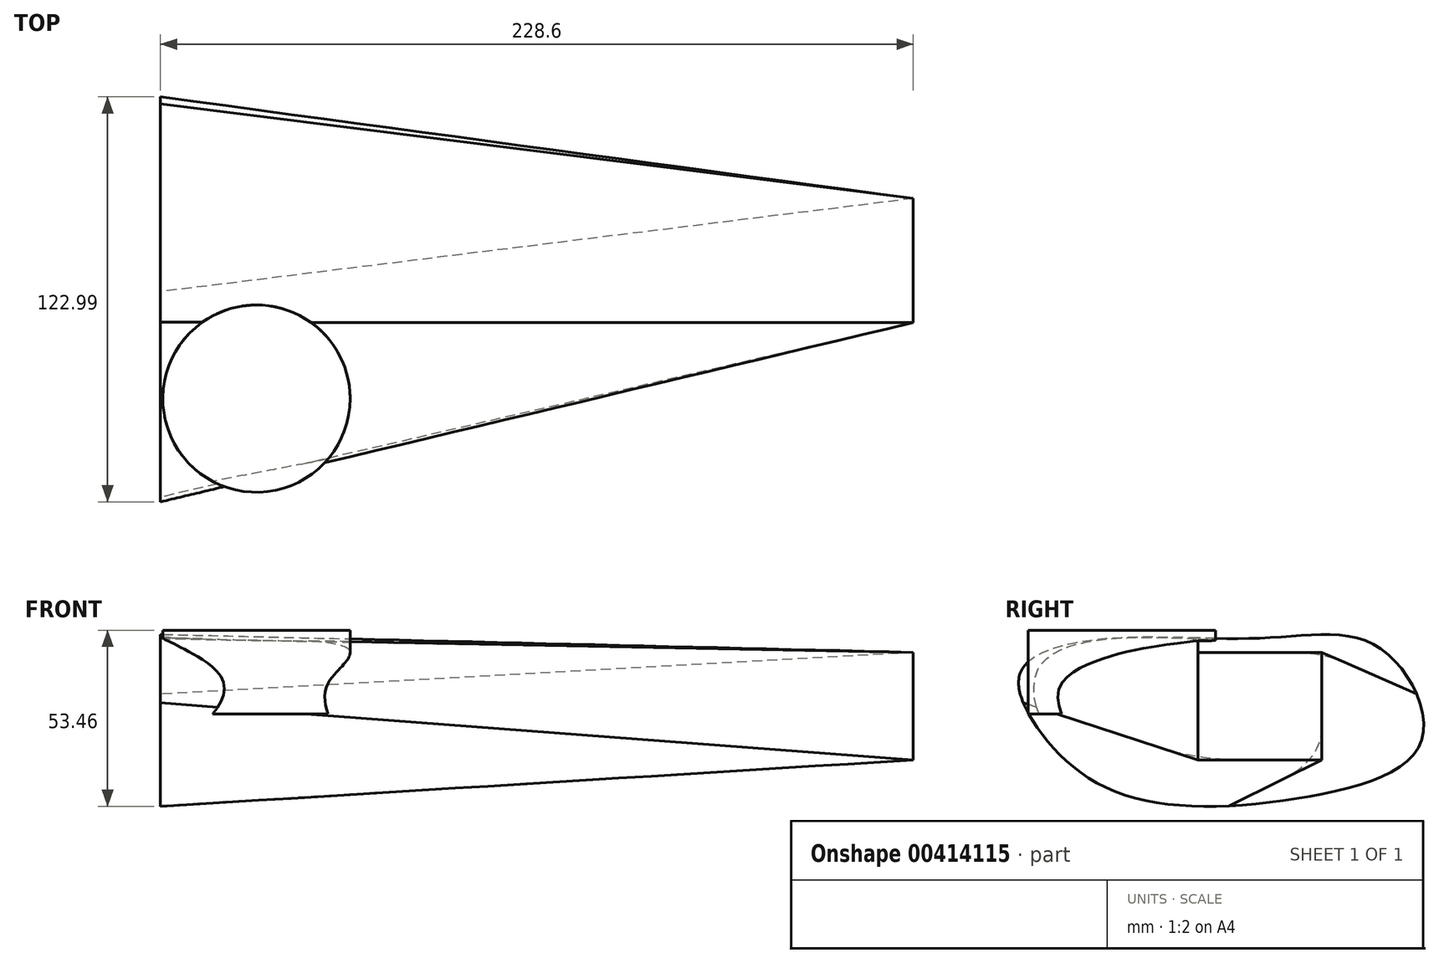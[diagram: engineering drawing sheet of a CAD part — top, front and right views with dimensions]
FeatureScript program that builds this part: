
annotation { "Feature Type Name" : "Feature", "Feature Type Description" : "" }
export const myFeature = defineFeature(function(context is Context, id is Id, definition is map)
    precondition{}
    {
        {
            var Q0;
            Q0=qCreatedBy(makeId("Right.planeOp"),FACE);
            cPlane(context, id + "F0", {"entities" : qUnion([Q0]), "cplaneType" : CPlaneType.OFFSET, "offset" : 228.6 * mm, "width" : 152.4 * mm, "height" : 152.4 * mm});
        }
        {
            var Q0;
            Q0=qCreatedBy(id+"F0.planeOp",FACE);
            var sketch = newSketch(context, id + "F1", { "sketchPlane" : qUnion([Q0])});
            skLineSegment(sketch, "E0.bottom", {"start": v(0, 18.7) * mm, "end": v(37.68, 18.7) * mm});
            skLineSegment(sketch, "E0.top", {"start": v(0, -14) * mm, "end": v(37.68, -14) * mm});
            skLineSegment(sketch, "E0.left", {"start": v(0, 18.7) * mm, "end": v(0, -14) * mm});
            skLineSegment(sketch, "E0.right", {"start": v(37.68, 18.7) * mm, "end": v(37.68, -14) * mm});
            skSolve(sketch);
        }
        {
            var Q0;
            Q0=qCreatedBy(makeId("Right.planeOp"),FACE);
            var sketch = newSketch(context, id + "F2", { "sketchPlane" : qUnion([Q0])});
            skFitSpline(sketch, "E1", {"points": [v(-49.04, -3.74) * mm, v(-22.8, -24.43) * mm, v(34.7, -24.88) * mm, v(68, -7.76) * mm, v(54.88, 20.24) * mm, v(20.58, 23.08) * mm, v(-28.86, 22.72) * mm, v(-53.58, 13.21) * mm, v(-49.04, -3.74) * mm]});
            skSolve(sketch);
        }
        {
            var Q0;
            Q0 = qSketchRegion(id + "F1", true);
            var Q1;
            Q1 = qSketchRegion(id + "F2", true);
            loft(context, id + "F3", {"sheetProfilesArray" : [{ "sheetProfileEntities" : qUnion([Q0]) }, { "sheetProfileEntities" : qUnion([Q1]) }]});
        }
        {
            var Q0;
            Q0=qCreatedBy(makeId("Top.planeOp"),FACE);
            var sketch = newSketch(context, id + "F4", { "sketchPlane" : qUnion([Q0])});
            skCircle(sketch, "E2", {"center": v(29.16, -23.07) * mm, "radius": 28.43 * mm});
            skSolve(sketch);
        }
        {
            var Q0;
            Q0=makeQuery(id+"F4.imprint","IMPRINT",FACE,{"disambiguationData":[TD([[makeQuery(id+"F4.imprint","IMPRINT",EDGE,{"derivedFrom":sQuery(id+"F4.wireOp",EDGE,"E2")}),1.0]])]});
            extrude(context, id + "F5", {"entities" : qUnion([Q0]), "operationType" : NewBodyOperationType.ADD, "depth" : 25.4 * mm});
        }
    });
